# Revit family: Haworth_Atwell_LoungeSeating
name_source: partatom
category: Furniture
revit_build: Autodesk Revit 2018 (Build: 20170223_1515(x64)
units: mm (PartAtom-declared; Revit-internal decimal feet)

## family parameters
Always vertical = Yes
Cut with Voids When Loaded = No
OmniClass Number = 23.40.20.00
OmniClass Title = General Furniture and Specialties
Room Calculation Point = No
Shared = No
Work Plane-Based = No

## types (3) — shared parameters
Actual Depth = 2' - 4 1/2"
Actual Height = 2' - 10"
Arm Cap = No
Assembly Code = E2020200
Manufacturer = Haworth
Model = Haworth Atwell
Size = Verify Final Dim. w/ Haworth
Sustainability Info = https://www.haworth.com
URL = http://healthcare.haworth.com
URL - Product = http://healthcare.haworth.com
Version = 0
Warranty = https://healthcare.haworth.com

## per-type parameters (varying)
| type | Actual Width | Chair | Description | Loveseat | Sofa |
| HE9022-LS - 56w | 4' - 8" | No | Love Seat Lounge | Yes | No |
| HE9011-AC - 33w | 2' - 9" | Yes | Single Seat Lounge | No | No |
| HE9033-SF - 79w | 6' - 7" | No | Three Seat Lounge | No | Yes |

## geometry (parser evidence)
native form markers: Sweep x2
no freeform markers — native parametric forms only
